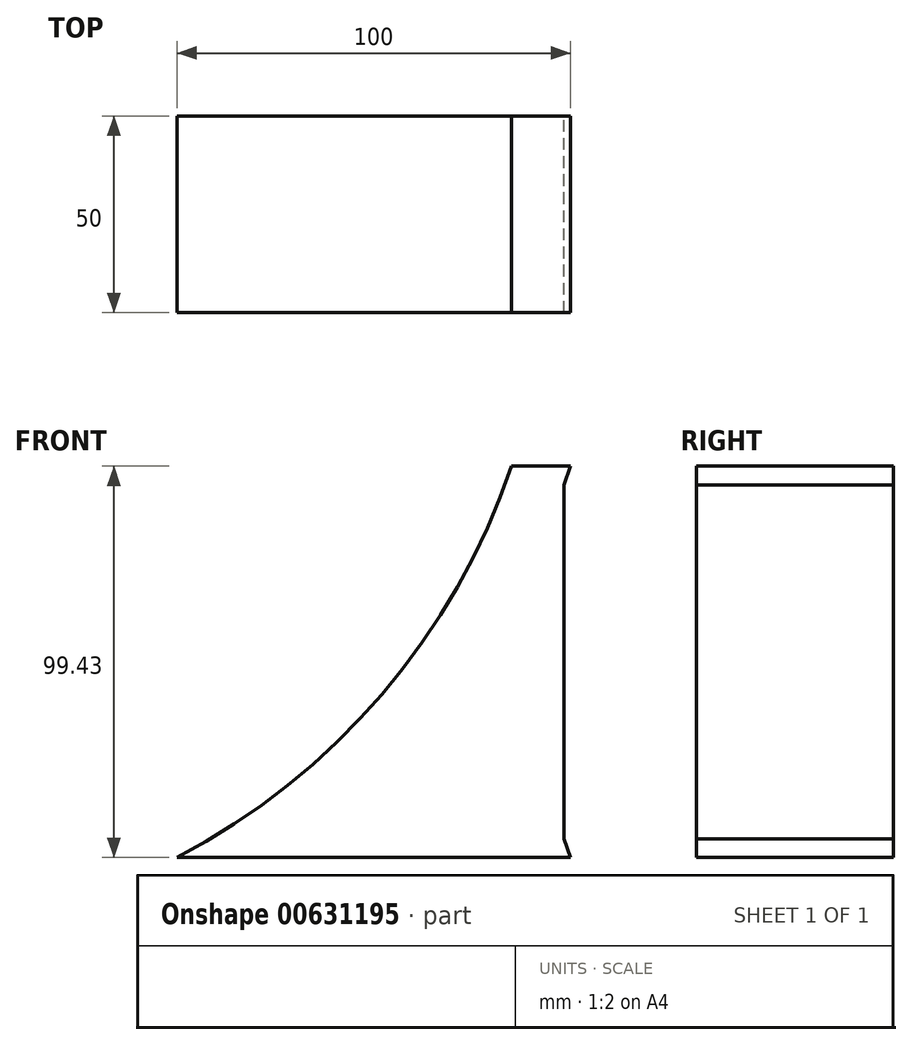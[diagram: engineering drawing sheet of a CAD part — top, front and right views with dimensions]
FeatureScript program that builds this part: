
annotation { "Feature Type Name" : "Feature", "Feature Type Description" : "" }
export const myFeature = defineFeature(function(context is Context, id is Id, definition is map)
    precondition{}
    {
        {
            var Q0;
            Q0=qCreatedBy(makeId("Front.planeOp"),FACE);
            var sketch = newSketch(context, id + "F0", { "sketchPlane" : qUnion([Q0])});
            skLineSegment(sketch, "E0", {"start": v(-51.14, -22.23) * mm, "end": v(48.86, -22.23) * mm});
            skLineSegment(sketch, "E1", {"start": v(48.86, -22.23) * mm, "end": v(47.2, -17.51) * mm});
            skLineSegment(sketch, "E2", {"start": v(47.2, -17.51) * mm, "end": v(47.2, 72.49) * mm});
            skLineSegment(sketch, "E3", {"start": v(47.2, 72.49) * mm, "end": v(48.86, 77.2) * mm});
            skLineSegment(sketch, "E4", {"start": v(48.86, 77.2) * mm, "end": v(33.86, 77.2) * mm});
            skArc(sketch, "E5", {"start": v(-51.14, -22.23) * mm, "mid": v(0.97, 19.27) * mm, "end": v(33.86, 77.2) * mm});
            skSolve(sketch);
        }
        {
            var Q0;
            Q0=makeQuery(id+"F0.imprint","IMPRINT",FACE,{"disambiguationData":[TD([[makeQuery(id+"F0.imprint","IMPRINT",EDGE,{"derivedFrom":sQuery(id+"F0.wireOp",EDGE,"E0")}),1.0]])]});
            extrude(context, id + "F1", {"entities" : qUnion([Q0]), "depth" : 50 * mm, "offsetDistance" : 25 * mm});
        }
    });
